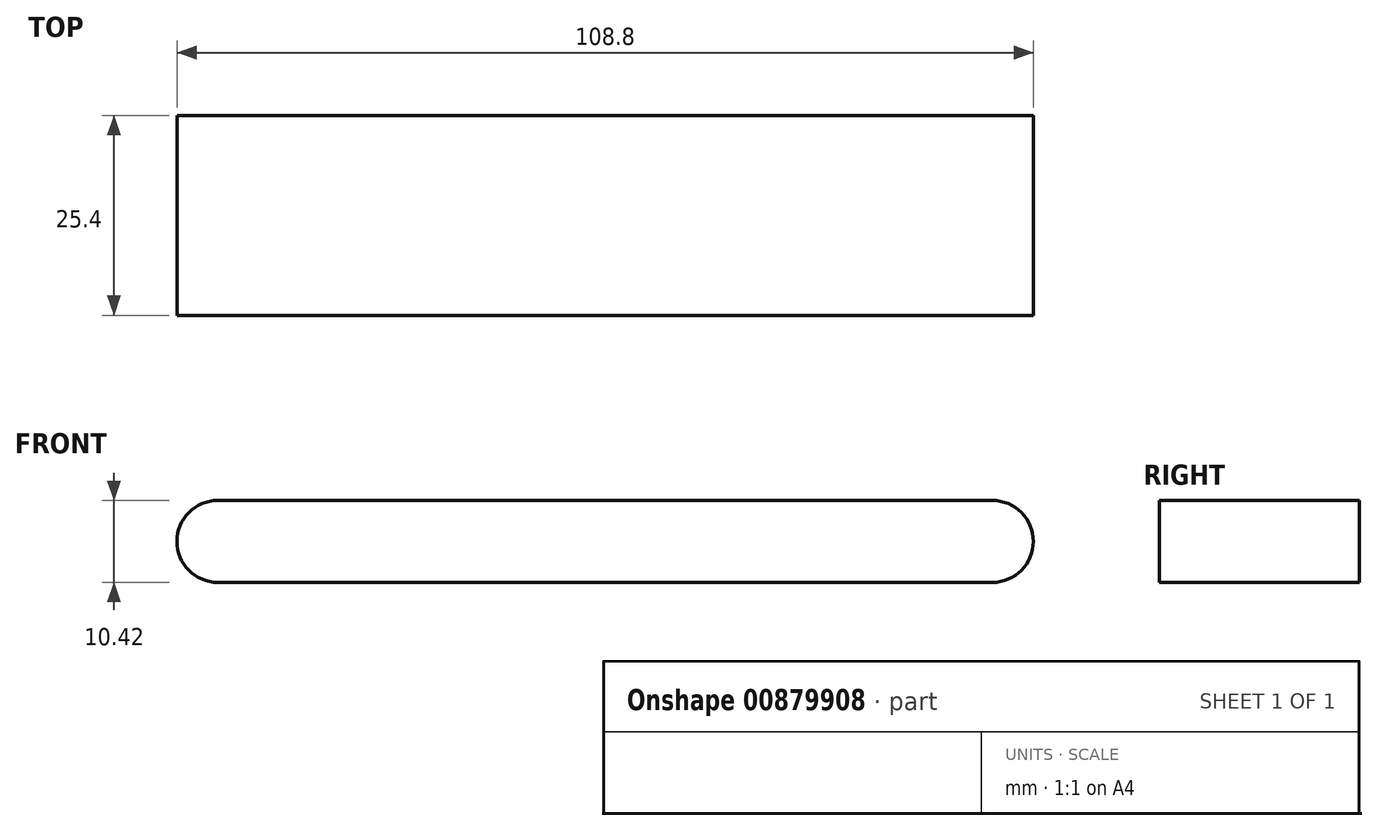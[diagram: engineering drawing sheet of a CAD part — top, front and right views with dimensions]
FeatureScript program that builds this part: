
annotation { "Feature Type Name" : "Feature", "Feature Type Description" : "" }
export const myFeature = defineFeature(function(context is Context, id is Id, definition is map)
    precondition{}
    {
        {
            var Q0;
            Q0=qCreatedBy(makeId("Front.planeOp"),FACE);
            var sketch = newSketch(context, id + "F0", { "sketchPlane" : qUnion([Q0])});
            skLineSegment(sketch, "E0", {"start": v(-54.84, 36.75) * mm, "end": v(43.55, 36.75) * mm});
            skLineSegment(sketch, "E1", {"start": v(-54.84, 26.33) * mm, "end": v(43.55, 26.33) * mm});
            skArc(sketch, "E2", {"start": v(-54.84, 36.75) * mm, "mid": v(-60.04, 31.54) * mm, "end": v(-54.84, 26.33) * mm});
            skArc(sketch, "E3", {"start": v(43.55, 26.33) * mm, "mid": v(48.76, 31.54) * mm, "end": v(43.55, 36.75) * mm});
            skSolve(sketch);
        }
        {
            var Q0;
            Q0 = qSketchRegion(id + "F0", true);
            extrude(context, id + "F1", {"entities" : qUnion([Q0]), "depth" : 25.4 * mm, "offsetDistance" : 25.4 * mm});
        }
    });
